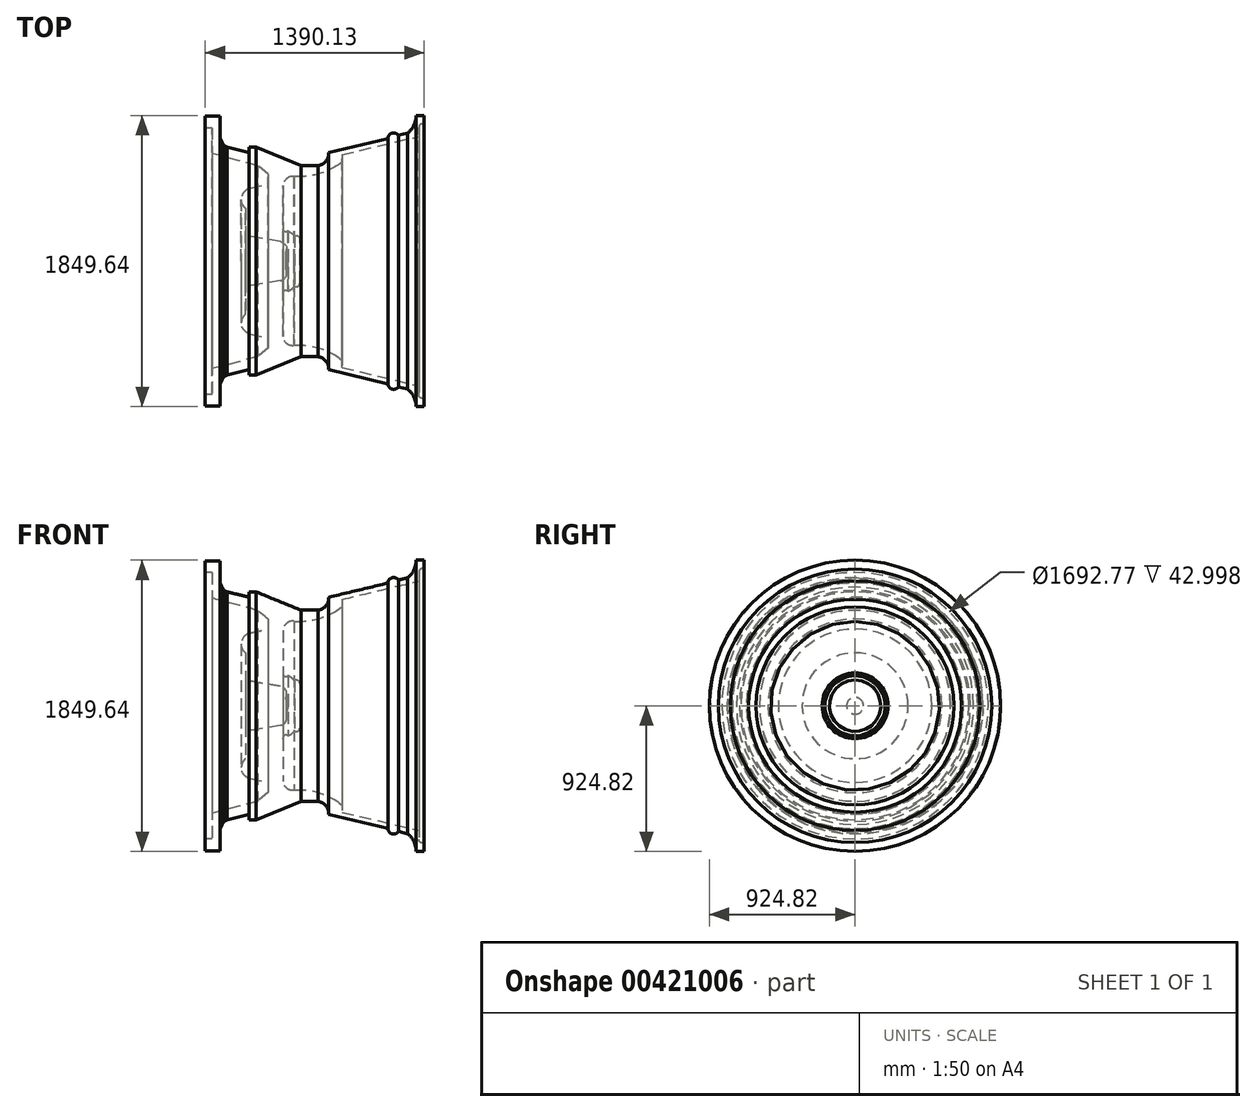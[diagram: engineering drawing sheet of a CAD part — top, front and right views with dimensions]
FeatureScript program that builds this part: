
annotation { "Feature Type Name" : "Feature", "Feature Type Description" : "" }
export const myFeature = defineFeature(function(context is Context, id is Id, definition is map)
    precondition{}
    {
        {
            var Q0;
            Q0=qCreatedBy(makeId("Front.planeOp"),FACE);
            var sketch = newSketch(context, id + "F0", { "sketchPlane" : qUnion([Q0])});
            skLineSegment(sketch, "E0", {"start": v(0, 0) * mm, "end": v(76.2, 0) * mm});
            skLineSegment(sketch, "E1", {"start": v(76.2, 0) * mm, "end": v(76.2, 139.7) * mm});
            skArc(sketch, "E2", {"start": v(76.2, 139.7) * mm, "mid": v(64.8, 159.8) * mm, "end": v(41.7, 160.37) * mm});
            skArc(sketch, "E3", {"start": v(41.7, 160.37) * mm, "mid": v(22.66, 178.3) * mm, "end": v(0, 191.36) * mm});
            skArc(sketch, "E4", {"start": v(-29.1, 209.2) * mm, "mid": v(-22.1, 187.96) * mm, "end": v(0, 191.36) * mm});
            skLineSegment(sketch, "E5", {"start": v(-29.1, 209.2) * mm, "end": v(-29.1, 478.95) * mm});
            skArc(sketch, "E6", {"start": v(39.9, 537.22) * mm, "mid": v(-8.12, 524.1) * mm, "end": v(-29.1, 478.95) * mm});
            skArc(sketch, "E7", {"start": v(39.9, 537.22) * mm, "mid": v(191.71, 552.9) * mm, "end": v(329.55, 618.42) * mm});
            skLineSegment(sketch, "E8", {"start": v(329.55, 618.42) * mm, "end": v(344.75, 629.15) * mm});
            skLineSegment(sketch, "E9", {"start": v(344.75, 629.15) * mm, "end": v(344.75, 675.71) * mm});
            skLineSegment(sketch, "E10", {"start": v(344.75, 675.71) * mm, "end": v(832.05, 792.32) * mm});
            skLineSegment(sketch, "E11", {"start": v(832.05, 792.32) * mm, "end": v(832.05, 849.56) * mm});
            skArc(sketch, "E12", {"start": v(865.43, 868.34) * mm, "mid": v(843.25, 868.7) * mm, "end": v(832.05, 849.56) * mm});
            skLineSegment(sketch, "E13", {"start": v(865.43, 868.34) * mm, "end": v(865.43, 924.82) * mm});
            skLineSegment(sketch, "E14", {"start": v(865.43, 924.82) * mm, "end": v(814.8, 924.82) * mm});
            skArc(sketch, "E15", {"start": v(761.52, 813.4) * mm, "mid": v(800.37, 863.26) * mm, "end": v(814.8, 924.82) * mm});
            skLineSegment(sketch, "E16", {"start": v(761.52, 813.4) * mm, "end": v(701.39, 799) * mm});
            skArc(sketch, "E17", {"start": v(701.39, 799) * mm, "mid": v(661.36, 813.15) * mm, "end": v(635.53, 779.46) * mm});
            skLineSegment(sketch, "E18", {"start": v(635.53, 779.46) * mm, "end": v(259.66, 689.52) * mm});
            skArc(sketch, "E19", {"start": v(192.23, 607.48) * mm, "mid": v(242.07, 635.25) * mm, "end": v(259.66, 689.52) * mm});
            skLineSegment(sketch, "E20", {"start": v(192.23, 607.48) * mm, "end": v(83.22, 607.48) * mm});
            skLineSegment(sketch, "E21", {"start": v(83.22, 607.48) * mm, "end": v(-201.82, 723.53) * mm});
            skLineSegment(sketch, "E22", {"start": v(-201.82, 723.53) * mm, "end": v(-244.82, 723.53) * mm});
            skLineSegment(sketch, "E23", {"start": v(-244.82, 723.53) * mm, "end": v(-244.82, 689.75) * mm});
            skLineSegment(sketch, "E24", {"start": v(-244.82, 689.75) * mm, "end": v(-386.1, 723.53) * mm});
            skLineSegment(sketch, "E25", {"start": v(-430.46, 800.31) * mm, "end": v(-430.46, 920.1) * mm});
            skLineSegment(sketch, "E26", {"start": v(-430.46, 920.1) * mm, "end": v(-524.7, 920.1) * mm});
            skLineSegment(sketch, "E27", {"start": v(-524.7, 920.1) * mm, "end": v(-524.7, 846.38) * mm});
            skLineSegment(sketch, "E28", {"start": v(-524.7, 846.38) * mm, "end": v(-481.7, 846.38) * mm});
            skLineSegment(sketch, "E29", {"start": v(-481.7, 846.38) * mm, "end": v(-481.7, 683.6) * mm});
            skLineSegment(sketch, "E30", {"start": v(-481.7, 683.6) * mm, "end": v(-193, 606.82) * mm});
            skLineSegment(sketch, "E31", {"start": v(-193, 606.82) * mm, "end": v(-125.43, 551.54) * mm});
            skLineSegment(sketch, "E32", {"start": v(-125.43, 551.54) * mm, "end": v(-125.43, 487.04) * mm});
            skLineSegment(sketch, "E33", {"start": v(-125.43, 487.04) * mm, "end": v(-239.07, 462.47) * mm});
            skArc(sketch, "E34", {"start": v(-239.07, 462.47) * mm, "mid": v(-293.84, 409.13) * mm, "end": v(-269.78, 336.55) * mm});
            skLineSegment(sketch, "E35", {"start": v(-269.78, 336.55) * mm, "end": v(-269.78, 161.49) * mm});
            skLineSegment(sketch, "E36", {"start": v(-269.78, 161.49) * mm, "end": v(-46.2, 123.47) * mm});
            skArc(sketch, "E37", {"start": v(-13, 53.52) * mm, "mid": v(-11.41, 97.13) * mm, "end": v(-46.2, 123.47) * mm});
            skLineSegment(sketch, "E38", {"start": v(-13, 53.52) * mm, "end": v(0, 0) * mm});
            skLineSegment(sketch, "E39", {"start": v(-430.46, 800.31) * mm, "end": v(-430.46, 782) * mm});
            skLineSegment(sketch, "E40", {"start": v(-430.46, 782) * mm, "end": v(-418.14, 753.6) * mm});
            skLineSegment(sketch, "E41", {"start": v(-418.14, 753.6) * mm, "end": v(-405.97, 733.32) * mm});
            skLineSegment(sketch, "E42", {"start": v(-405.97, 733.32) * mm, "end": v(-386.1, 723.53) * mm});
            skSolve(sketch);
        }
        {
            var Q0;
            Q0=makeQuery(id+"F0.imprint","IMPRINT",FACE,{"disambiguationData":[TD([[makeQuery(id+"F0.imprint","IMPRINT",EDGE,{"derivedFrom":sQuery(id+"F0.wireOp",EDGE,"E0")}),1.0]])]});
            var Q1;
            Q1=sQuery(id+"F0.wireOp",EDGE,"E0");
            revolve(context, id + "F1", {"entities" : qUnion([Q0]), "axis" : qUnion([Q1]), "revolveType" : RevolveType.FULL});
        }
    });
